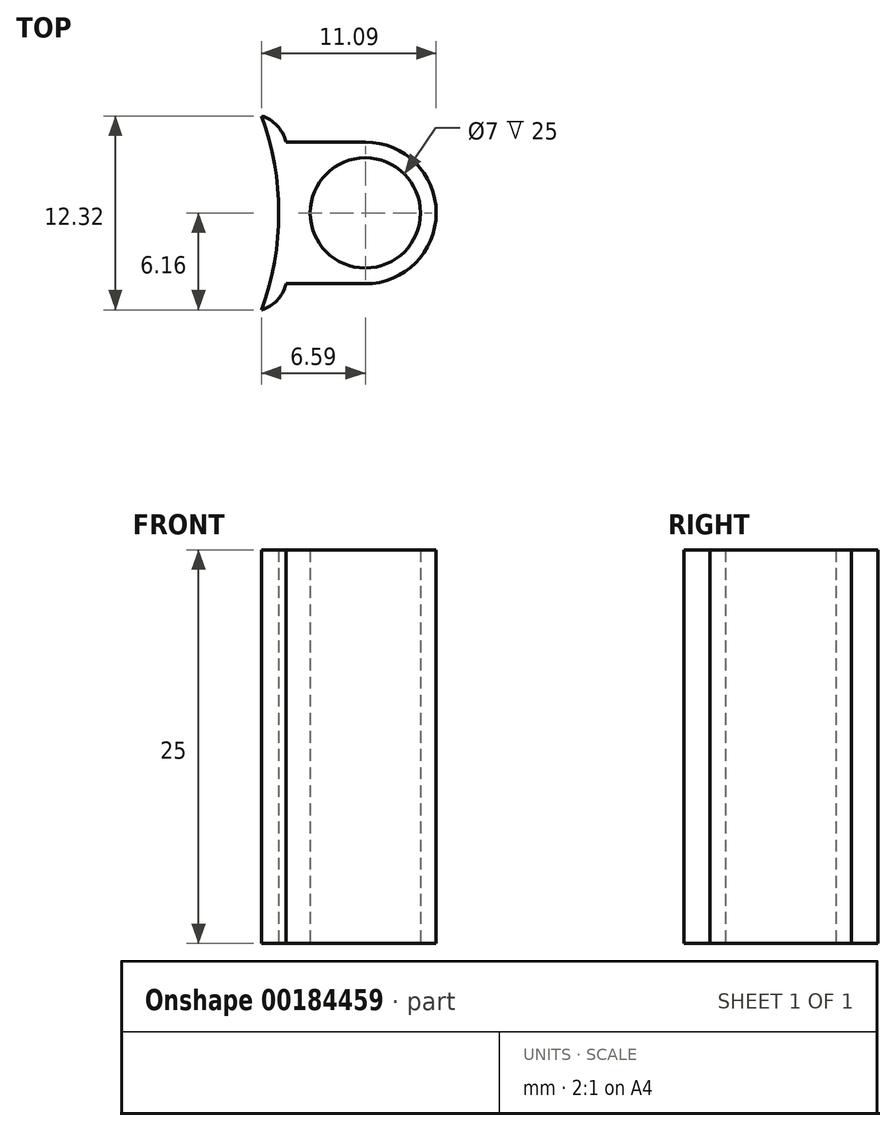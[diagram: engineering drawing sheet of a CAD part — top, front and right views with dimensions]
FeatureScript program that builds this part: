
annotation { "Feature Type Name" : "Feature", "Feature Type Description" : "" }
export const myFeature = defineFeature(function(context is Context, id is Id, definition is map)
    precondition{}
    {
        {
            var Q0;
            Q0=qCreatedBy(makeId("Top.planeOp"),FACE);
            var sketch = newSketch(context, id + "F0", { "sketchPlane" : qUnion([Q0])});
            skCircle(sketch, "E0", {"center": v(0, 0) * mm, "radius": 19 * mm});
            skCircle(sketch, "E1", {"center": v(23.5, 0) * mm, "radius": 4.5 * mm});
            skCircle(sketch, "E2", {"center": v(23.5, 0) * mm, "radius": 3.5 * mm});
            skLineSegment(sketch, "E3", {"start": v(23.5, -4.5) * mm, "end": v(18.46, -4.5) * mm});
            skLineSegment(sketch, "E4", {"start": v(23.5, 4.5) * mm, "end": v(18.46, 4.5) * mm});
            skLineSegment(sketch, "E5", {"start": v(0, 0) * mm, "end": v(17.85, -6.5) * mm});
            skLineSegment(sketch, "E6", {"start": v(0, 0) * mm, "end": v(17.85, 6.5) * mm});
            skCircle(sketch, "E7", {"center": v(0, 0) * mm, "radius": 18 * mm});
            skPoint(sketch, "E8", {"position": v(16.91, -6.16) * mm});
            skPoint(sketch, "E9", {"position": v(16.91, 6.16) * mm});
            skSolve(sketch);
        }
        {
            var Q0;
            Q0=makeQuery(id+"F0.imprint","IMPRINT",FACE,{"disambiguationData":[TD([[makeQuery(id+"F0.imprint","IMPRINT",EDGE,{"derivedFrom":sQuery(id+"F0.wireOp",EDGE,"E2")}),-1.0]])]});
            var Q1;
            {var subQ0=sQuery(id+"F0.wireOp",EDGE,"E4");Q1=makeQuery(id+"F0.imprint","IMPRINT",FACE,{"disambiguationData":[TD([[makeQuery(id+"F0.imprint","IMPRINT",EDGE,{"derivedFrom":subQ0}),1.0]])]});}
            var Q2;
            {var subQ0=sQuery(id+"F0.wireOp",EDGE,"E3");Q2=makeQuery(id+"F0.imprint","IMPRINT",FACE,{"disambiguationData":[TD([[makeQuery(id+"F0.imprint","IMPRINT",EDGE,{"derivedFrom":subQ0}),-1.0]])]});}
            var Q3;
            {var subQ0=sQuery(id+"F0.wireOp",EDGE,"E0");var subQ5=makeQuery(id+"F0.imprint","INTERSECT",VERTEX,{"derivedFrom":[subQ0,sQuery(id+"F0.wireOp",EDGE,"E4")]});Q3=makeQuery(id+"F0.imprint","IMPRINT",FACE,{"disambiguationData":[TD([[makeQuery(id+"F0.imprint","IMPRINT",EDGE,{"disambiguationData":[TD([[subQ5,1.0]])],"derivedFrom":subQ0}),1.0]])]});}
            extrude(context, id + "F1", {"entities" : qUnion([Q0, Q1, Q2, Q3]), "depth" : 25 * mm});
        }
        {
            var Q0;
            Q0=makeQuery(id+"F1.opExtrude","SWEPT_EDGE",EDGE,{"disambiguationData":[OSD([sQuery(id+"F0.wireOp",EDGE,"E0"),sQuery(id+"F0.wireOp",EDGE,"E5")])]});
            var Q1;
            Q1=makeQuery(id+"F1.opExtrude","SWEPT_EDGE",EDGE,{"disambiguationData":[OSD([sQuery(id+"F0.wireOp",EDGE,"E0"),sQuery(id+"F0.wireOp",EDGE,"E6")])]});
            fillet(context, id + "F2", {"entities" : qUnion([Q0, Q1]), "radius" : 2.25 * mm, "tangentPropagation" : true, "allowEdgeOverflow" : false});
        }
    });
